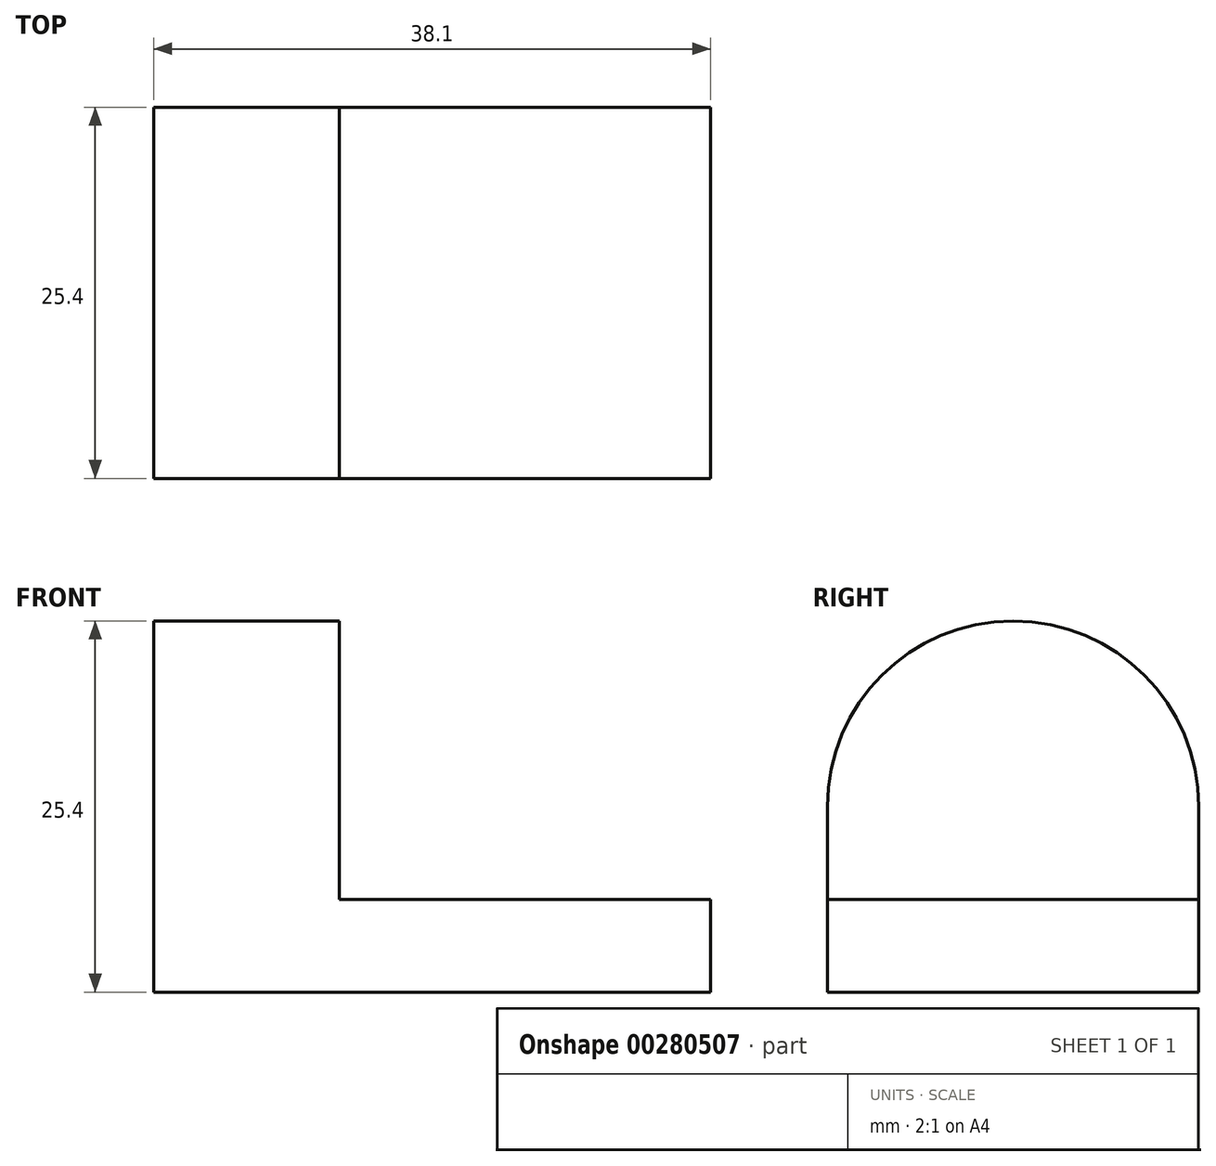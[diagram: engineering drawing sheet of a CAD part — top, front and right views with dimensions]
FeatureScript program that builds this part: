
annotation { "Feature Type Name" : "Feature", "Feature Type Description" : "" }
export const myFeature = defineFeature(function(context is Context, id is Id, definition is map)
    precondition{}
    {
        {
            var Q0;
            Q0=qCreatedBy(makeId("Right.planeOp"),FACE);
            var sketch = newSketch(context, id + "F0", { "sketchPlane" : qUnion([Q0])});
            skLineSegment(sketch, "E0", {"start": v(0, 0) * mm, "end": v(0, 12.7) * mm});
            skLineSegment(sketch, "E1", {"start": v(25.4, 0) * mm, "end": v(25.4, 12.7) * mm});
            skLineSegment(sketch, "E2", {"start": v(25.4, 12.7) * mm, "end": v(25.4, 0) * mm});
            skLineSegment(sketch, "E3", {"start": v(0, 0) * mm, "end": v(25.4, 0) * mm});
            skArc(sketch, "E4", {"start": v(25.4, 12.7) * mm, "mid": v(12.7, 25.4) * mm, "end": v(0, 12.7) * mm});
            skSolve(sketch);
        }
        {
            var Q0;
            Q0 = qSketchRegion(id + "F0", true);
            extrude(context, id + "F1", {"entities" : qUnion([Q0]), "depth" : 38.1 * mm});
        }
        {
            var Q0;
            Q0=makeQuery(id+"F1.opExtrude","CAP_FACE",FACE,{"disambiguationData":[OSD([sQuery(id+"F0.wireOp",EDGE,"E0"),sQuery(id+"F0.wireOp",EDGE,"E2"),sQuery(id+"F0.wireOp",EDGE,"E3"),sQuery(id+"F0.wireOp",EDGE,"E4")])],"isStart":false});
            var sketch = newSketch(context, id + "F2", { "sketchPlane" : qUnion([Q0])});
            skLineSegment(sketch, "E5.bottom", {"start": v(0, 6.35) * mm, "end": v(25.4, 6.35) * mm});
            skLineSegment(sketch, "E5.top", {"start": v(0, 31.75) * mm, "end": v(25.4, 31.75) * mm});
            skLineSegment(sketch, "E5.left", {"start": v(0, 6.35) * mm, "end": v(0, 31.75) * mm});
            skLineSegment(sketch, "E5.right", {"start": v(25.4, 6.35) * mm, "end": v(25.4, 31.75) * mm});
            skSolve(sketch);
        }
        {
            var Q0;
            Q0 = qSketchRegion(id + "F2", true);
            extrude(context, id + "F3", {"entities" : qUnion([Q0]), "operationType" : NewBodyOperationType.REMOVE, "oppositeDirection" : true, "depth" : 25.4 * mm});
        }
    });
